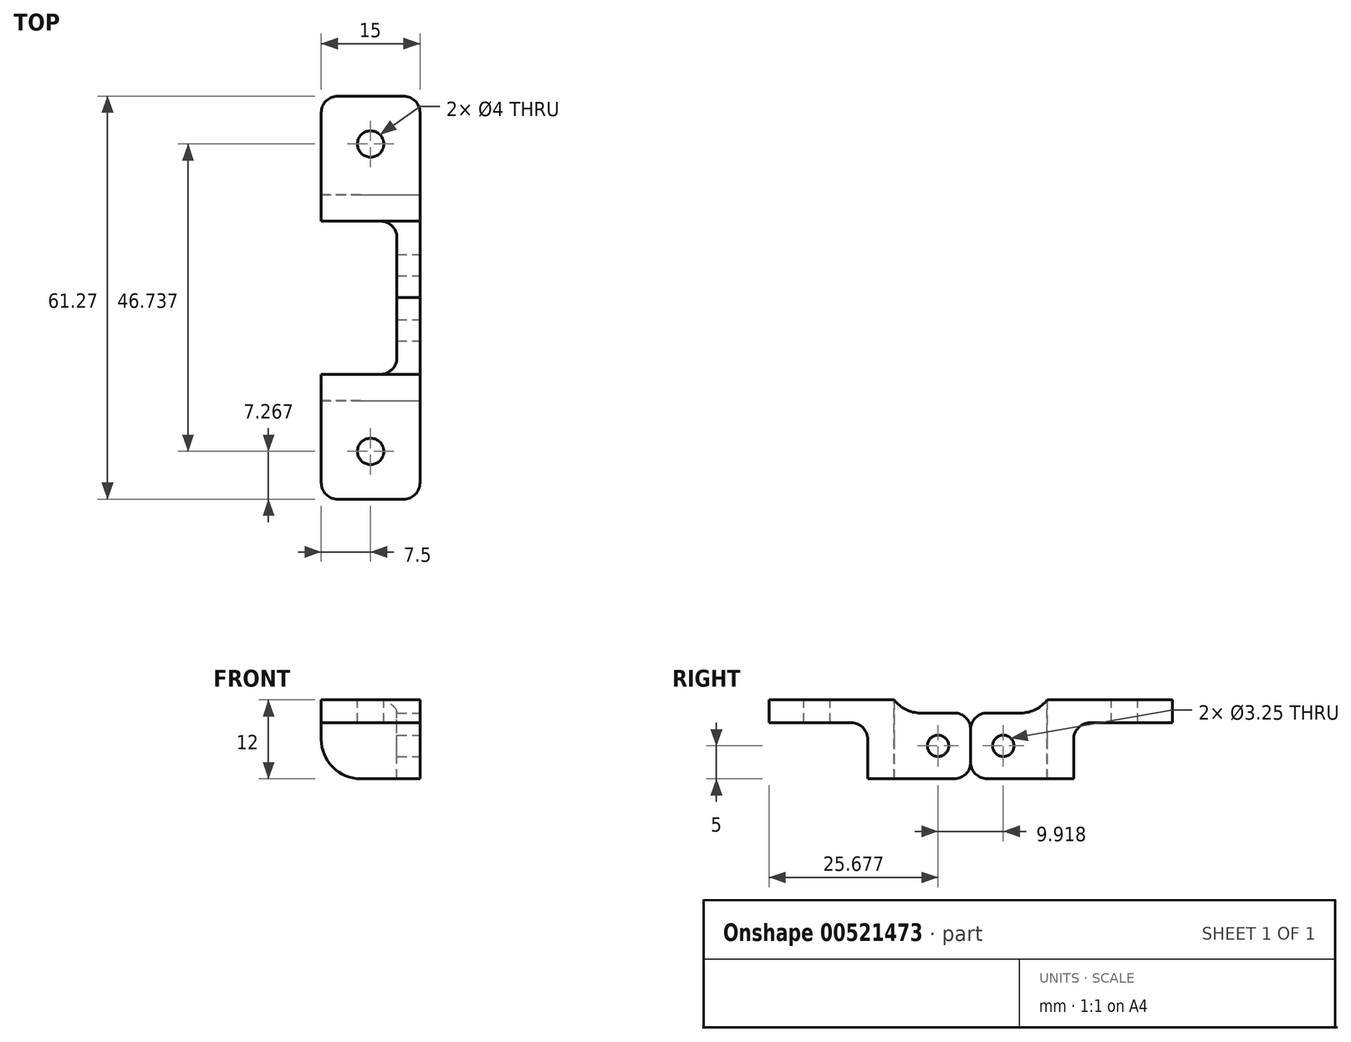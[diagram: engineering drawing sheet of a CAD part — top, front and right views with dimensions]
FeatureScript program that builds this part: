
annotation { "Feature Type Name" : "Feature", "Feature Type Description" : "" }
export const myFeature = defineFeature(function(context is Context, id is Id, definition is map)
    precondition{}
    {
        {
            var Q0;
            Q0=qCreatedBy(makeId("Right.planeOp"),FACE);
            var sketch = newSketch(context, id + "F0", { "sketchPlane" : qUnion([Q0])});
            skLineSegment(sketch, "E0", {"start": v(-19, 0) * mm, "end": v(0, 0) * mm});
            skLineSegment(sketch, "E1", {"start": v(0, 0) * mm, "end": v(0, -2) * mm});
            skLineSegment(sketch, "E2", {"start": v(0, -2) * mm, "end": v(11.64, -2) * mm});
            skLineSegment(sketch, "E3", {"start": v(11.64, -2) * mm, "end": v(11.64, -12) * mm});
            skLineSegment(sketch, "E4", {"start": v(11.64, -12) * mm, "end": v(-4, -12) * mm});
            skLineSegment(sketch, "E5", {"start": v(-4, -12) * mm, "end": v(-4, -3.5) * mm});
            skLineSegment(sketch, "E6", {"start": v(-4, -3.5) * mm, "end": v(-19, -3.5) * mm});
            skLineSegment(sketch, "E7", {"start": v(-19, -3.5) * mm, "end": v(-19, 0) * mm});
            skCircle(sketch, "E8", {"center": v(6.68, -7) * mm, "radius": 1.63 * mm});
            skPoint(sketch, "E9", {"position": v(11.64, -7) * mm});
            skSolve(sketch);
        }
        {
            var Q0;
            Q0=makeQuery(id+"F0.imprint","IMPRINT",FACE,{"disambiguationData":[TD([[makeQuery(id+"F0.imprint","IMPRINT",EDGE,{"derivedFrom":sQuery(id+"F0.wireOp",EDGE,"E0")}),-1.0]])]});
            extrude(context, id + "F1", {"entities" : qUnion([Q0]), "oppositeDirection" : true, "depth" : 15 * mm, "offsetDistance" : 25 * mm});
        }
        {
            var Q0;
            Q0=makeQuery(id+"F1.opExtrude","SWEPT_FACE",FACE,{"disambiguationData":[OSD([sQuery(id+"F0.wireOp",EDGE,"E2")])]});
            var sketch = newSketch(context, id + "F2", { "sketchPlane" : qUnion([Q0])});
            skLineSegment(sketch, "E10.bottom", {"start": v(-15, 0) * mm, "end": v(-3.5, 0) * mm});
            skLineSegment(sketch, "E10.top", {"start": v(-15, 11.64) * mm, "end": v(-3.5, 11.64) * mm});
            skLineSegment(sketch, "E10.left", {"start": v(-15, 0) * mm, "end": v(-15, 11.64) * mm});
            skLineSegment(sketch, "E10.right", {"start": v(-3.5, 0) * mm, "end": v(-3.5, 11.64) * mm});
            skSolve(sketch);
        }
        {
            var Q0;
            Q0=makeQuery(id+"F2.imprint","IMPRINT",FACE,{"disambiguationData":[TD([[makeQuery(id+"F2.imprint","IMPRINT",EDGE,{"derivedFrom":sQuery(id+"F2.wireOp",EDGE,"E10.bottom")}),1.0]])]});
            extrude(context, id + "F3", {"entities" : qUnion([Q0]), "operationType" : NewBodyOperationType.REMOVE, "oppositeDirection" : true, "depth" : 25 * mm, "offsetDistance" : 25 * mm});
        }
        {
            var Q0;
            Q0=makeQuery(id+"F1.opExtrude","SWEPT_FACE",FACE,{"disambiguationData":[OSD([sQuery(id+"F0.wireOp",EDGE,"E0")])]});
            var sketch = newSketch(context, id + "F4", { "sketchPlane" : qUnion([Q0])});
            skCircle(sketch, "E11", {"center": v(-7.5, -11.73) * mm, "radius": 2 * mm});
            skPoint(sketch, "E11.centerSnap0", {"position": v(-7.5, -19) * mm});
            skSolve(sketch);
        }
        {
            var Q0;
            Q0=makeQuery(id+"F4.imprint","IMPRINT",FACE,{"disambiguationData":[TD([[makeQuery(id+"F4.imprint","IMPRINT",EDGE,{"derivedFrom":sQuery(id+"F4.wireOp",EDGE,"E11")}),1.0]])]});
            extrude(context, id + "F5", {"entities" : qUnion([Q0]), "operationType" : NewBodyOperationType.REMOVE, "oppositeDirection" : true, "depth" : 25 * mm, "offsetDistance" : 25 * mm});
        }
        {
            var Q0;
            Q0=makeQuery(id+"F1.opExtrude","CAP_EDGE",EDGE,{"disambiguationData":[OSD([sQuery(id+"F0.wireOp",EDGE,"E7")])],"isStart":true});
            var Q1;
            Q1=makeQuery(id+"F1.opExtrude","CAP_EDGE",EDGE,{"disambiguationData":[OSD([sQuery(id+"F0.wireOp",EDGE,"E7")])],"isStart":false});
            var Q2;
            Q2=makeQuery(id+"F1.opExtrude","SWEPT_EDGE",EDGE,{"disambiguationData":[OSD([sQuery(id+"F0.wireOp",EDGE,"E2"),sQuery(id+"F0.wireOp",EDGE,"E3")])]});
            var Q3;
            Q3=makeQuery(id+"F1.opExtrude","SWEPT_EDGE",EDGE,{"disambiguationData":[OSD([sQuery(id+"F0.wireOp",EDGE,"E3"),sQuery(id+"F0.wireOp",EDGE,"E4")])]});
            fillet(context, id + "F6", {"entities" : qUnion([Q0, Q1, Q2, Q3]), "radius" : 2.5 * mm, "tangentPropagation" : true, "allowEdgeOverflow" : false});
        }
        {
            var Q0;
            Q0=makeQuery(id+"F1.opExtrude","SWEPT_EDGE",EDGE,{"disambiguationData":[OSD([sQuery(id+"F0.wireOp",EDGE,"E1"),sQuery(id+"F0.wireOp",EDGE,"E2")])]});
            fillet(context, id + "F7", {"entities" : qUnion([Q0]), "radius" : 5 * mm, "tangentPropagation" : true, "allowEdgeOverflow" : false});
        }
        {
            var Q0;
            Q0=makeQuery(id+"F1.opExtrude","SWEPT_EDGE",EDGE,{"disambiguationData":[OSD([sQuery(id+"F0.wireOp",EDGE,"E5"),sQuery(id+"F0.wireOp",EDGE,"E6")])]});
            fillet(context, id + "F8", {"entities" : qUnion([Q0]), "radius" : 2.5 * mm, "tangentPropagation" : true, "allowEdgeOverflow" : false});
        }
        {
            var Q0;
            Q0=makeQuery(id+"F1.opExtrude","CAP_EDGE",EDGE,{"disambiguationData":[OSD([sQuery(id+"F0.wireOp",EDGE,"E4")])],"isStart":false});
            fillet(context, id + "F9", {"entities" : qUnion([Q0]), "radius" : 6 * mm, "tangentPropagation" : true, "allowEdgeOverflow" : false});
        }
        {
            var Q0;
            Q0=makeQuery(id+"F3.boolean.opBoolean","COPY",EDGE,{"derivedFrom":makeQuery(id+"F3.opExtrude","SWEPT_EDGE",EDGE,{"disambiguationData":[OSD([sQuery(id+"F0.wireOp",EDGE,"E1"),sQuery(id+"F0.wireOp",EDGE,"E2"),sQuery(id+"F2.wireOp",EDGE,"E10.bottom"),sQuery(id+"F2.wireOp",EDGE,"E10.right")])]})});
            fillet(context, id + "F10", {"entities" : qUnion([Q0]), "radius" : 2.5 * mm, "tangentPropagation" : true, "allowEdgeOverflow" : false});
        }
        {
            var Q0;
            Q0=makeQuery(id+"F1.opExtrude","SWEPT_BODY",BODY,{"disambiguationData":[OSD([sQuery(id+"F0.wireOp",EDGE,"E0"),sQuery(id+"F0.wireOp",EDGE,"E1"),sQuery(id+"F0.wireOp",EDGE,"E2"),sQuery(id+"F0.wireOp",EDGE,"E3"),sQuery(id+"F0.wireOp",EDGE,"E4"),sQuery(id+"F0.wireOp",EDGE,"E5"),sQuery(id+"F0.wireOp",EDGE,"E6"),sQuery(id+"F0.wireOp",EDGE,"E7"),sQuery(id+"F0.wireOp",EDGE,"E8")])]});
            var Q1;
            Q1=makeQuery(id+"F1.opExtrude","SWEPT_FACE",FACE,{"disambiguationData":[OSD([sQuery(id+"F0.wireOp",EDGE,"E3")])]});
            mirror(context, id + "F11", {"entities" : qUnion([Q0]), "mirrorPlane" : qUnion([Q1])});
        }
    });
